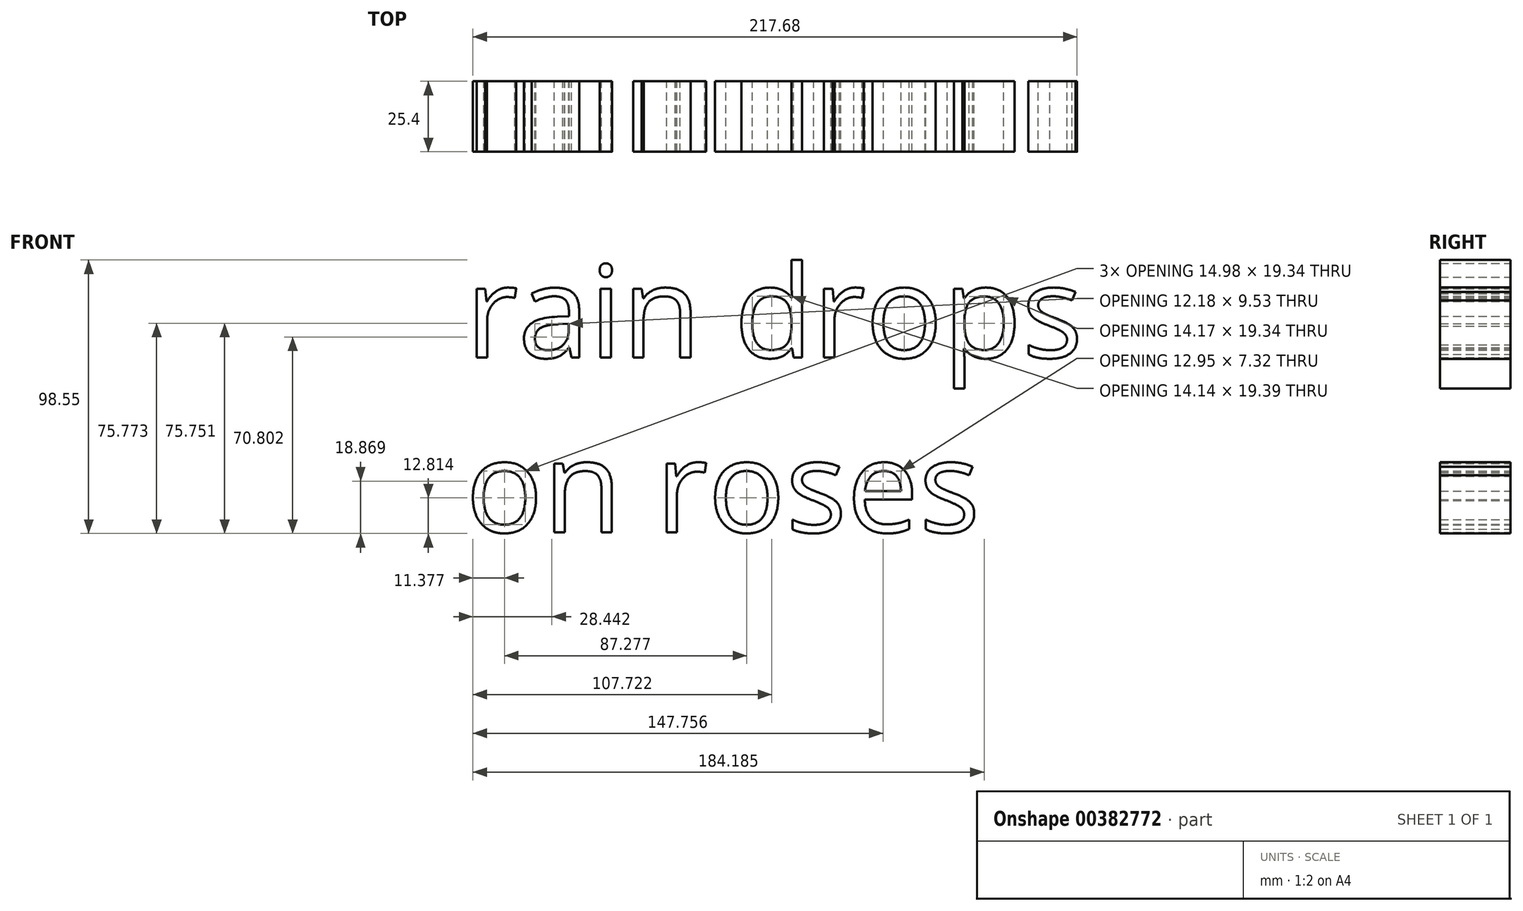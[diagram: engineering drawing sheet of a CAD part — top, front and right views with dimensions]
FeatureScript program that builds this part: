
annotation { "Feature Type Name" : "Feature", "Feature Type Description" : "" }
export const myFeature = defineFeature(function(context is Context, id is Id, definition is map)
    precondition{}
    {
        {
            var Q0;
            Q0=qCreatedBy(makeId("Front.planeOp"),FACE);
            var sketch = newSketch(context, id + "F0", { "sketchPlane" : qUnion([Q0])});
            skText(sketch, "E0", { "text": "rain drops\non roses", "fontName": "OpenSans-Regular.ttf"});
            const initialGuessF0  = {"E0": [-0.0829, -0.02872, 1, 0, 0.03332]};
            skSetInitialGuess(sketch, initialGuessF0);
            skSolve(sketch);
        }
        {
            var Q0;
            Q0 = qSketchRegion(id + "F0", true);
            extrude(context, id + "F1", {"entities" : qUnion([Q0]), "depth" : 25.4 * mm});
        }
    });
